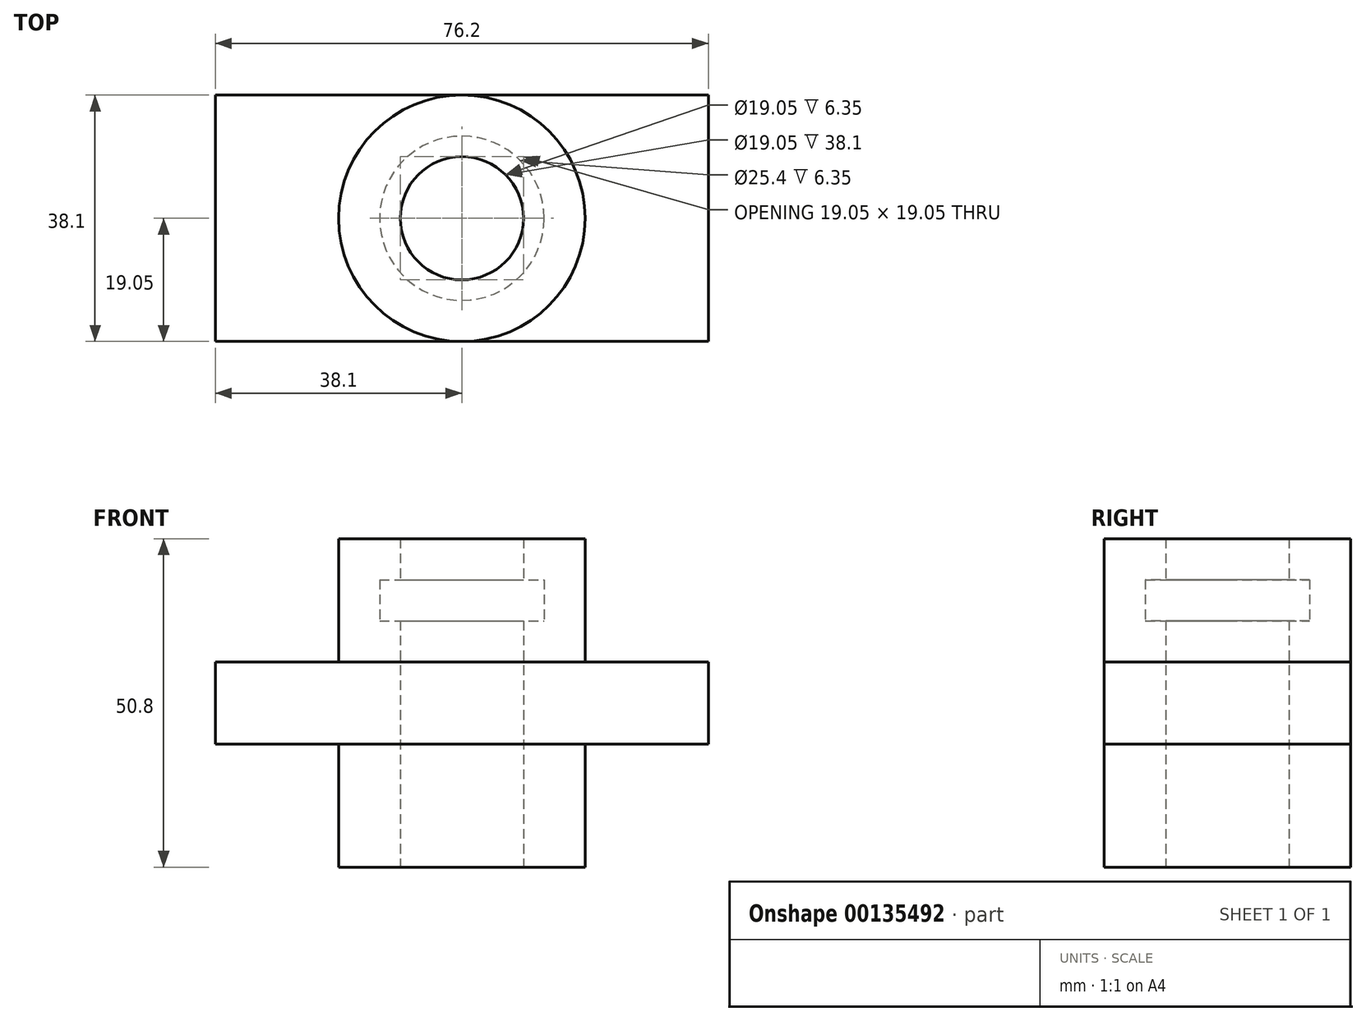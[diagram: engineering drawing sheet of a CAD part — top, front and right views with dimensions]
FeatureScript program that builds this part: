
annotation { "Feature Type Name" : "Feature", "Feature Type Description" : "" }
export const myFeature = defineFeature(function(context is Context, id is Id, definition is map)
    precondition{}
    {
        {
            var Q0;
            Q0=qCreatedBy(makeId("Front.planeOp"),FACE);
            var sketch = newSketch(context, id + "F0", { "sketchPlane" : qUnion([Q0])});
            skLineSegment(sketch, "E0", {"start": v(-38.1, 6.35) * mm, "end": v(-38.1, -6.35) * mm});
            skLineSegment(sketch, "E1", {"start": v(-38.1, -6.35) * mm, "end": v(38.1, -6.35) * mm});
            skLineSegment(sketch, "E2", {"start": v(38.1, -6.35) * mm, "end": v(38.1, 6.35) * mm});
            skLineSegment(sketch, "E3", {"start": v(38.1, 6.35) * mm, "end": v(-38.1, 6.35) * mm});
            skSolve(sketch);
        }
        {
            var Q0;
            Q0 = qSketchRegion(id + "F0", true);
            extrude(context, id + "F1", {"entities" : qUnion([Q0]), "endBound" : BoundingType.SYMMETRIC, "depth" : 38.1 * mm});
        }
        {
            var Q0;
            Q0=makeQuery(id+"F1.opExtrude","SWEPT_FACE",FACE,{"disambiguationData":[OSD([sQuery(id+"F0.wireOp",EDGE,"E3")])]});
            var sketch = newSketch(context, id + "F2", { "sketchPlane" : qUnion([Q0])});
            skCircle(sketch, "E4", {"center": v(0, 0) * mm, "radius": 19.05 * mm});
            skCircle(sketch, "E5", {"center": v(0, 0) * mm, "radius": 9.53 * mm});
            skSolve(sketch);
        }
        {
            var Q0;
            Q0=makeQuery(id+"F2.imprint","IMPRINT",FACE,{"disambiguationData":[TD([[makeQuery(id+"F2.imprint","IMPRINT",EDGE,{"derivedFrom":sQuery(id+"F2.wireOp",EDGE,"E5")}),-1.0]])]});
            extrude(context, id + "F3", {"entities" : qUnion([Q0]), "operationType" : NewBodyOperationType.ADD, "depth" : 19.05 * mm, "hasSecondDirection" : true, "secondDirectionOppositeDirection" : true, "secondDirectionDepth" : 31.75 * mm});
        }
        {
            var Q0;
            Q0=makeQuery(id+"F3.boolean.opBoolean","SPLIT",FACE,{"disambiguationData":[TD([makeQuery(id+"F3.opExtrude","SWEPT_FACE",FACE,{"disambiguationData":[OSD([sQuery(id+"F2.wireOp",EDGE,"E5")])]})])],"derivedFrom":makeQuery(id+"F1.opExtrude","SWEPT_FACE",FACE,{"disambiguationData":[OSD([sQuery(id+"F0.wireOp",EDGE,"E3")])]})});
            extrude(context, id + "F4", {"entities" : qUnion([Q0]), "operationType" : NewBodyOperationType.REMOVE, "oppositeDirection" : true, "depth" : 76.2 * mm});
        }
        {
            var Q0;
            Q0=qCreatedBy(makeId("Front.planeOp"),FACE);
            var sketch = newSketch(context, id + "F5", { "sketchPlane" : qUnion([Q0])});
            skLineSegment(sketch, "E6.bottom", {"start": v(0, 19.05) * mm, "end": v(12.7, 19.05) * mm});
            skLineSegment(sketch, "E6.top", {"start": v(0, 12.7) * mm, "end": v(12.7, 12.7) * mm});
            skLineSegment(sketch, "E6.left", {"start": v(0, 19.05) * mm, "end": v(0, 12.7) * mm});
            skLineSegment(sketch, "E6.right", {"start": v(12.7, 19.05) * mm, "end": v(12.7, 12.7) * mm});
            skSolve(sketch);
        }
        {
            var Q0;
            Q0=makeQuery(id+"F5.imprint","IMPRINT",FACE,{"disambiguationData":[TD([[makeQuery(id+"F5.imprint","IMPRINT",EDGE,{"derivedFrom":sQuery(id+"F5.wireOp",EDGE,"E6.bottom")}),-1.0]])]});
            var Q1;
            Q1=sQuery(id+"F5.wireOp",EDGE,"E6.left");
            revolve(context, id + "F6", {"operationType" : NewBodyOperationType.REMOVE, "entities" : qUnion([Q0]), "axis" : qUnion([Q1]), "revolveType" : RevolveType.FULL, "oppositeDirection" : true});
        }
    });
